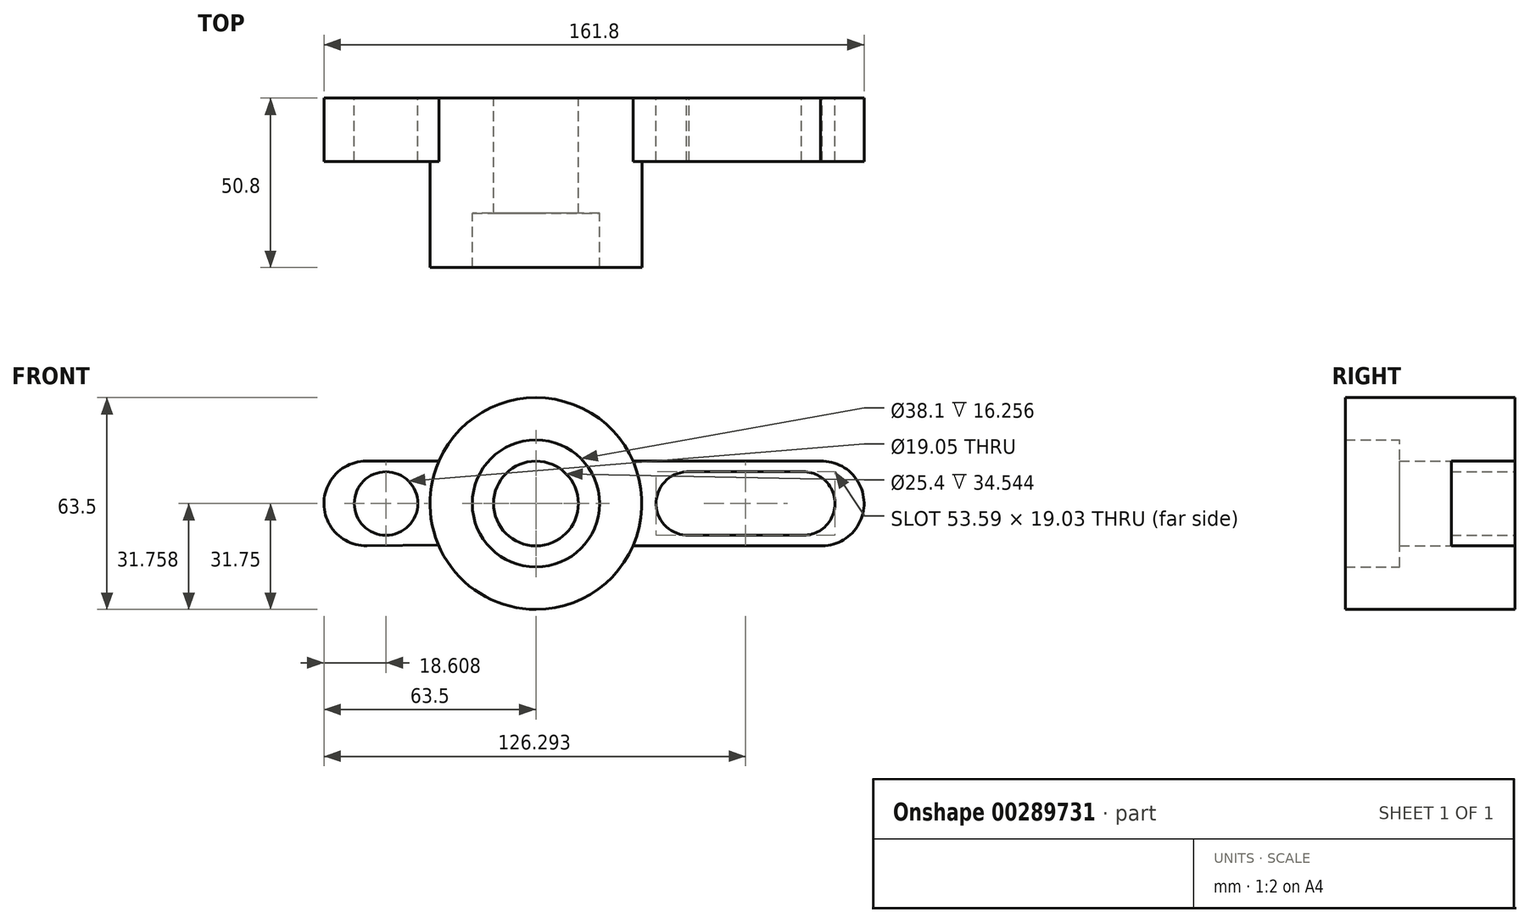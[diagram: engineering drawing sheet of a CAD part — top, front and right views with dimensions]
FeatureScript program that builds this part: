
annotation { "Feature Type Name" : "Feature", "Feature Type Description" : "" }
export const myFeature = defineFeature(function(context is Context, id is Id, definition is map)
    precondition{}
    {
        {
            var Q0;
            Q0=qCreatedBy(makeId("Front.planeOp"),FACE);
            var sketch = newSketch(context, id + "F0", { "sketchPlane" : qUnion([Q0])});
            skCircle(sketch, "E0", {"center": v(0, 0) * mm, "radius": 12.7 * mm});
            skCircle(sketch, "E1", {"center": v(0, 0) * mm, "radius": 19.05 * mm});
            skCircle(sketch, "E2", {"center": v(0, 0) * mm, "radius": 31.75 * mm});
            skArc(sketch, "E3", {"start": v(-50.7, 12.7) * mm, "mid": v(-63.5, -0.03) * mm, "end": v(-50.65, -12.7) * mm});
            skArc(sketch, "E4", {"start": v(85.37, -12.7) * mm, "mid": v(98.3, 0.04) * mm, "end": v(85.28, 12.7) * mm});
            skLineSegment(sketch, "E5", {"start": v(-50.9, 12.7) * mm, "end": v(-29.1, 12.7) * mm});
            skLineSegment(sketch, "E6", {"start": v(-50.65, -12.7) * mm, "end": v(-29.21, -12.44) * mm});
            skLineSegment(sketch, "E7", {"start": v(85.28, 12.7) * mm, "end": v(29.1, 12.7) * mm});
            skLineSegment(sketch, "E8", {"start": v(85.83, -12.7) * mm, "end": v(29.1, -12.7) * mm});
            skArc(sketch, "E9", {"start": v(45.1, 9.5) * mm, "mid": v(36, -0.4) * mm, "end": v(45.89, -9.5) * mm});
            skCircle(sketch, "E10", {"center": v(-44.9, 0) * mm, "radius": 9.53 * mm});
            skArc(sketch, "E11", {"start": v(79.5, -9.5) * mm, "mid": v(89.59, -0.28) * mm, "end": v(80.06, 9.52) * mm});
            skLineSegment(sketch, "E12", {"start": v(45.1, 9.5) * mm, "end": v(80.06, 9.52) * mm});
            skLineSegment(sketch, "E13", {"start": v(45.12, -9.5) * mm, "end": v(80.63, -9.5) * mm});
            skSolve(sketch);
        }
        {
            var Q0;
            Q0=makeQuery(id+"F0.imprint","IMPRINT",FACE,{"disambiguationData":[TD([[makeQuery(id+"F0.imprint","IMPRINT",EDGE,{"derivedFrom":sQuery(id+"F0.wireOp",EDGE,"E1")}),-1.0]])]});
            extrude(context, id + "F1", {"entities" : qUnion([Q0]), "depth" : 50.8 * mm});
        }
        {
            var Q0;
            {var subQ6=sQuery(id+"F0.wireOp",EDGE,"E6");Q0=makeQuery(id+"F0.imprint","IMPRINT",FACE,{"disambiguationData":[TD([[makeQuery(id+"F0.imprint","IMPRINT",EDGE,{"derivedFrom":subQ6}),1.0]])]});}
            var Q1;
            {var subQ13=sQuery(id+"F0.wireOp",EDGE,"E7");Q1=makeQuery(id+"F0.imprint","IMPRINT",FACE,{"disambiguationData":[TD([[makeQuery(id+"F0.imprint","IMPRINT",EDGE,{"derivedFrom":subQ13}),1.0]])]});}
            extrude(context, id + "F2", {"entities" : qUnion([Q0, Q1]), "operationType" : NewBodyOperationType.ADD, "depth" : 19.05 * mm});
        }
        {
            var Q0;
            Q0=makeQuery(id+"F0.imprint","IMPRINT",FACE,{"disambiguationData":[TD([[makeQuery(id+"F0.imprint","IMPRINT",EDGE,{"derivedFrom":sQuery(id+"F0.wireOp",EDGE,"E0")}),-1.0]])]});
            extrude(context, id + "F3", {"entities" : qUnion([Q0]), "operationType" : NewBodyOperationType.ADD, "depth" : 34.54 * mm});
        }
    });
